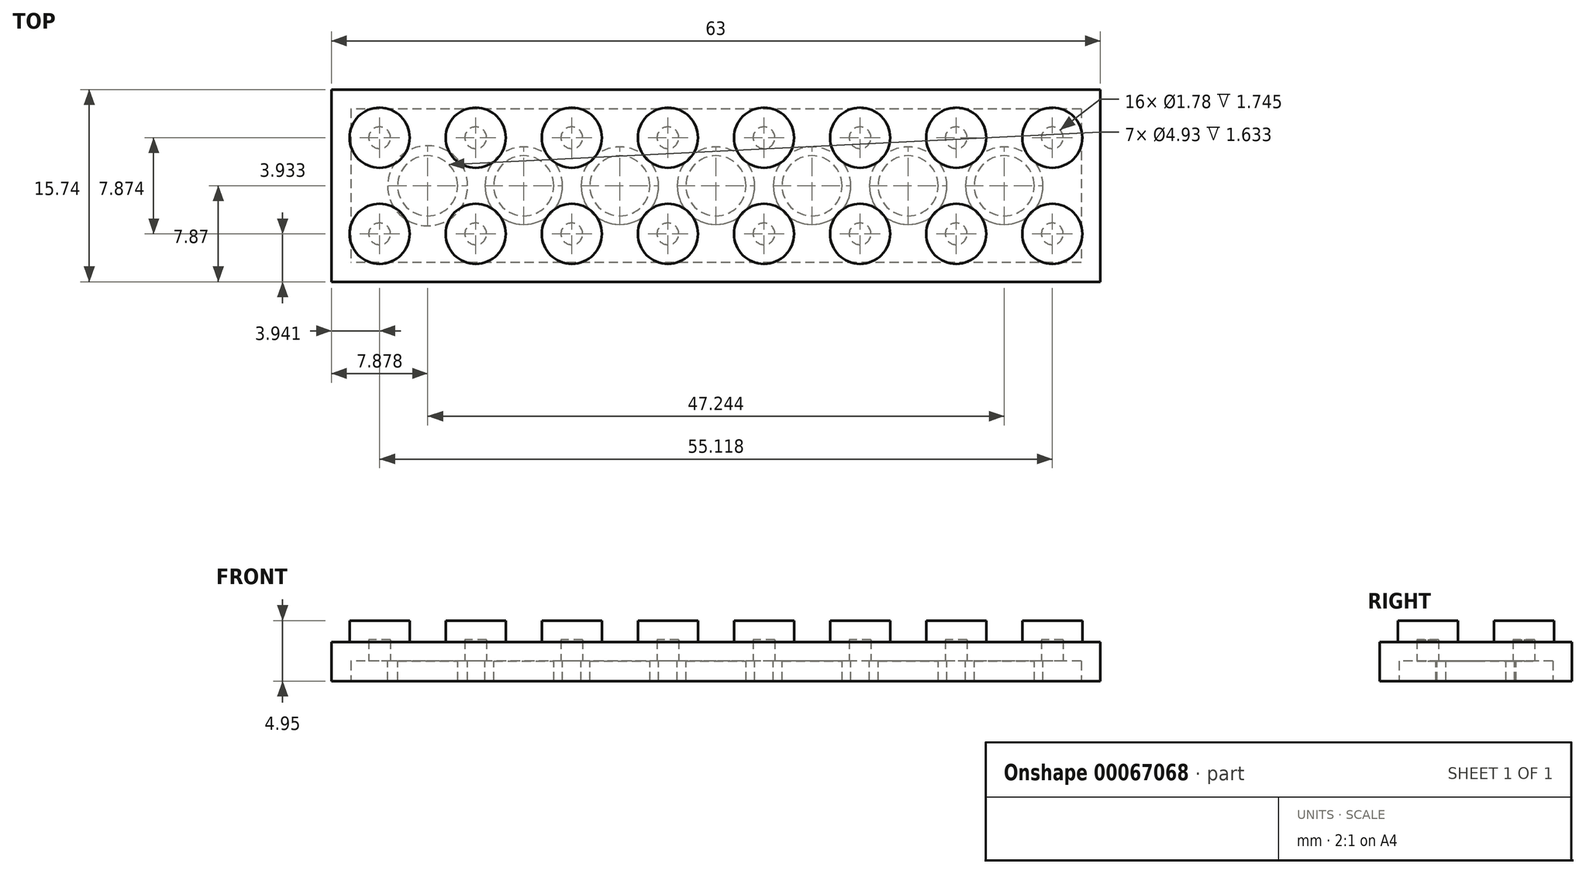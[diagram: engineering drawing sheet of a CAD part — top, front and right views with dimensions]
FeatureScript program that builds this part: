
annotation { "Feature Type Name" : "Feature", "Feature Type Description" : "" }
export const myFeature = defineFeature(function(context is Context, id is Id, definition is map)
    precondition{}
    {
        {
            var Q0;
            Q0=qCreatedBy(makeId("Top.planeOp"),FACE);
            var sketch = newSketch(context, id + "F0", { "sketchPlane" : qUnion([Q0])});
            skLineSegment(sketch, "E0.rect.bottom", {"start": v(31.5, 7.87) * mm, "end": v(-31.5, 7.87) * mm});
            skLineSegment(sketch, "E0.rect.top", {"start": v(31.5, -7.87) * mm, "end": v(-31.5, -7.87) * mm});
            skLineSegment(sketch, "E0.rect.left", {"start": v(31.5, 7.87) * mm, "end": v(31.5, -7.87) * mm});
            skLineSegment(sketch, "E0.rect.right", {"start": v(-31.5, 7.87) * mm, "end": v(-31.5, -7.87) * mm});
            skPoint(sketch, "E0.rect.middle", {"position": v(0, 0) * mm});
            skSolve(sketch);
        }
        {
            var Q0;
            Q0=makeQuery(id+"F0.imprint","IMPRINT",FACE,{"disambiguationData":[TD([[makeQuery(id+"F0.imprint","IMPRINT",EDGE,{"derivedFrom":sQuery(id+"F0.wireOp",EDGE,"E0.rect.bottom")}),1.0]])]});
            extrude(context, id + "F1", {"entities" : qUnion([Q0]), "depth" : 3.2 * mm});
        }
        {
            var Q0;
            Q0=qCreatedBy(makeId("Top.planeOp"),FACE);
            var sketch = newSketch(context, id + "F2", { "sketchPlane" : qUnion([Q0])});
            skCircle(sketch, "E1", {"center": v(-27.56, 3.94) * mm, "radius": 2.46 * mm});
            skCircle(sketch, "E2", {"center": v(-19.69, 3.94) * mm, "radius": 2.46 * mm});
            skCircle(sketch, "E3", {"center": v(-11.81, 3.94) * mm, "radius": 2.46 * mm});
            skCircle(sketch, "E4", {"center": v(-3.94, 3.94) * mm, "radius": 2.46 * mm});
            skCircle(sketch, "E5", {"center": v(-3.94, -3.94) * mm, "radius": 2.46 * mm});
            skCircle(sketch, "E6", {"center": v(-11.81, -3.94) * mm, "radius": 2.46 * mm});
            skCircle(sketch, "E7", {"center": v(-19.69, -3.94) * mm, "radius": 2.46 * mm});
            skCircle(sketch, "E8", {"center": v(-27.56, -3.94) * mm, "radius": 2.46 * mm});
            skCircle(sketch, "E9", {"center": v(3.94, 3.94) * mm, "radius": 2.46 * mm});
            skCircle(sketch, "E10", {"center": v(11.81, 3.94) * mm, "radius": 2.46 * mm});
            skCircle(sketch, "E11", {"center": v(11.81, -3.94) * mm, "radius": 2.46 * mm});
            skCircle(sketch, "E12", {"center": v(3.94, -3.94) * mm, "radius": 2.46 * mm});
            skCircle(sketch, "E13", {"center": v(19.69, 3.94) * mm, "radius": 2.46 * mm});
            skCircle(sketch, "E14", {"center": v(27.56, 3.94) * mm, "radius": 2.46 * mm});
            skCircle(sketch, "E15", {"center": v(19.69, -3.94) * mm, "radius": 2.46 * mm});
            skCircle(sketch, "E16", {"center": v(27.56, -3.94) * mm, "radius": 2.46 * mm});
            skSolve(sketch);
        }
        {
            var Q0;
            Q0=makeQuery(id+"F2.imprint","IMPRINT",FACE,{"disambiguationData":[TD([[makeQuery(id+"F2.imprint","IMPRINT",EDGE,{"derivedFrom":sQuery(id+"F2.wireOp",EDGE,"E14")}),1.0]])]});
            var Q1;
            Q1=makeQuery(id+"F2.imprint","IMPRINT",FACE,{"disambiguationData":[TD([[makeQuery(id+"F2.imprint","IMPRINT",EDGE,{"derivedFrom":sQuery(id+"F2.wireOp",EDGE,"E10")}),1.0]])]});
            var Q2;
            Q2=makeQuery(id+"F2.imprint","IMPRINT",FACE,{"disambiguationData":[TD([[makeQuery(id+"F2.imprint","IMPRINT",EDGE,{"derivedFrom":sQuery(id+"F2.wireOp",EDGE,"E13")}),1.0]])]});
            var Q3;
            Q3=makeQuery(id+"F2.imprint","IMPRINT",FACE,{"disambiguationData":[TD([[makeQuery(id+"F2.imprint","IMPRINT",EDGE,{"derivedFrom":sQuery(id+"F2.wireOp",EDGE,"E9")}),1.0]])]});
            var Q4;
            Q4=makeQuery(id+"F2.imprint","IMPRINT",FACE,{"disambiguationData":[TD([[makeQuery(id+"F2.imprint","IMPRINT",EDGE,{"derivedFrom":sQuery(id+"F2.wireOp",EDGE,"E4")}),1.0]])]});
            var Q5;
            Q5=makeQuery(id+"F2.imprint","IMPRINT",FACE,{"disambiguationData":[TD([[makeQuery(id+"F2.imprint","IMPRINT",EDGE,{"derivedFrom":sQuery(id+"F2.wireOp",EDGE,"E3")}),1.0]])]});
            var Q6;
            Q6=makeQuery(id+"F2.imprint","IMPRINT",FACE,{"disambiguationData":[TD([[makeQuery(id+"F2.imprint","IMPRINT",EDGE,{"derivedFrom":sQuery(id+"F2.wireOp",EDGE,"E2")}),1.0]])]});
            var Q7;
            Q7=makeQuery(id+"F2.imprint","IMPRINT",FACE,{"disambiguationData":[TD([[makeQuery(id+"F2.imprint","IMPRINT",EDGE,{"derivedFrom":sQuery(id+"F2.wireOp",EDGE,"E1")}),1.0]])]});
            var Q8;
            Q8=makeQuery(id+"F2.imprint","IMPRINT",FACE,{"disambiguationData":[TD([[makeQuery(id+"F2.imprint","IMPRINT",EDGE,{"derivedFrom":sQuery(id+"F2.wireOp",EDGE,"E8")}),1.0]])]});
            var Q9;
            Q9=makeQuery(id+"F2.imprint","IMPRINT",FACE,{"disambiguationData":[TD([[makeQuery(id+"F2.imprint","IMPRINT",EDGE,{"derivedFrom":sQuery(id+"F2.wireOp",EDGE,"E7")}),1.0]])]});
            var Q10;
            Q10=makeQuery(id+"F2.imprint","IMPRINT",FACE,{"disambiguationData":[TD([[makeQuery(id+"F2.imprint","IMPRINT",EDGE,{"derivedFrom":sQuery(id+"F2.wireOp",EDGE,"E6")}),1.0]])]});
            var Q11;
            Q11=makeQuery(id+"F2.imprint","IMPRINT",FACE,{"disambiguationData":[TD([[makeQuery(id+"F2.imprint","IMPRINT",EDGE,{"derivedFrom":sQuery(id+"F2.wireOp",EDGE,"E5")}),1.0]])]});
            var Q12;
            Q12=makeQuery(id+"F2.imprint","IMPRINT",FACE,{"disambiguationData":[TD([[makeQuery(id+"F2.imprint","IMPRINT",EDGE,{"derivedFrom":sQuery(id+"F2.wireOp",EDGE,"E12")}),1.0]])]});
            var Q13;
            Q13=makeQuery(id+"F2.imprint","IMPRINT",FACE,{"disambiguationData":[TD([[makeQuery(id+"F2.imprint","IMPRINT",EDGE,{"derivedFrom":sQuery(id+"F2.wireOp",EDGE,"E11")}),1.0]])]});
            var Q14;
            Q14=makeQuery(id+"F2.imprint","IMPRINT",FACE,{"disambiguationData":[TD([[makeQuery(id+"F2.imprint","IMPRINT",EDGE,{"derivedFrom":sQuery(id+"F2.wireOp",EDGE,"E15")}),1.0]])]});
            var Q15;
            Q15=makeQuery(id+"F2.imprint","IMPRINT",FACE,{"disambiguationData":[TD([[makeQuery(id+"F2.imprint","IMPRINT",EDGE,{"derivedFrom":sQuery(id+"F2.wireOp",EDGE,"E16")}),1.0]])]});
            extrude(context, id + "F3", {"entities" : qUnion([Q0, Q1, Q2, Q3, Q4, Q5, Q6, Q7, Q8, Q9, Q10, Q11, Q12, Q13, Q14, Q15]), "operationType" : NewBodyOperationType.ADD, "depth" : 4.95 * mm});
        }
        {
            var Q0;
            Q0=makeQuery(id+"F1.opExtrude","CAP_FACE",FACE,{"disambiguationData":[OSD([sQuery(id+"F0.wireOp",EDGE,"E0.rect.bottom"),sQuery(id+"F0.wireOp",EDGE,"E0.rect.top"),sQuery(id+"F0.wireOp",EDGE,"E0.rect.left"),sQuery(id+"F0.wireOp",EDGE,"E0.rect.right")])],"isStart":true});
            shell(context, id + "F4", {"entities" : qUnion([Q0]), "thickness" : 1.57 * mm});
        }
        {
            var Q0;
            Q0=makeQuery(id+"F4.opShell","OFFSET_FACE",FACE,{"disambiguationData":[OSD([sQuery(id+"F0.wireOp",EDGE,"E0.rect.bottom"),sQuery(id+"F0.wireOp",EDGE,"E0.rect.top"),sQuery(id+"F0.wireOp",EDGE,"E0.rect.left"),sQuery(id+"F0.wireOp",EDGE,"E0.rect.right")])]});
            var sketch = newSketch(context, id + "F5", { "sketchPlane" : qUnion([Q0])});
            skCircle(sketch, "E17", {"center": v(0, 0) * mm, "radius": 2.46 * mm});
            skLineSegment(sketch, "E18", {"start": v(0, 0) * mm, "end": v(7.87, 0) * mm});
            skLineSegment(sketch, "E19", {"start": v(7.87, 0) * mm, "end": v(15.75, 0) * mm});
            skLineSegment(sketch, "E20", {"start": v(15.75, 0) * mm, "end": v(23.62, 0) * mm});
            skLineSegment(sketch, "E21", {"start": v(0, 0) * mm, "end": v(-7.87, 0) * mm});
            skLineSegment(sketch, "E22", {"start": v(-7.87, 0) * mm, "end": v(-15.75, 0) * mm});
            skLineSegment(sketch, "E23", {"start": v(-15.75, 0) * mm, "end": v(-23.62, 0) * mm});
            skCircle(sketch, "E24", {"center": v(-7.87, 0) * mm, "radius": 2.46 * mm});
            skCircle(sketch, "E25", {"center": v(-15.75, 0) * mm, "radius": 2.46 * mm});
            skCircle(sketch, "E26", {"center": v(-23.62, 0) * mm, "radius": 2.46 * mm});
            skCircle(sketch, "E27", {"center": v(7.87, 0) * mm, "radius": 2.46 * mm});
            skCircle(sketch, "E28", {"center": v(15.75, 0) * mm, "radius": 2.46 * mm});
            skCircle(sketch, "E29", {"center": v(23.62, 0) * mm, "radius": 2.46 * mm});
            skCircle(sketch, "E30", {"center": v(-23.62, 0) * mm, "radius": 3.28 * mm});
            skCircle(sketch, "E31", {"center": v(-15.75, 0) * mm, "radius": 3.18 * mm});
            skCircle(sketch, "E32", {"center": v(-7.87, 0) * mm, "radius": 3.18 * mm});
            skCircle(sketch, "E33", {"center": v(0, 0) * mm, "radius": 3.18 * mm});
            skCircle(sketch, "E34", {"center": v(7.87, 0) * mm, "radius": 3.18 * mm});
            skCircle(sketch, "E35", {"center": v(15.75, 0) * mm, "radius": 3.18 * mm});
            skCircle(sketch, "E36", {"center": v(23.62, 0) * mm, "radius": 3.18 * mm});
            skSolve(sketch);
        }
        {
            var Q0;
            Q0=makeQuery(id+"F5.imprint","IMPRINT",FACE,{"disambiguationData":[TD([[makeQuery(id+"F5.imprint","IMPRINT",EDGE,{"derivedFrom":sQuery(id+"F5.wireOp",EDGE,"E26")}),-1.0]])]});
            var Q1;
            {var subQ0=sQuery(id+"F5.wireOp",EDGE,"E31");var subQ1=sQuery(id+"F5.wireOp",EDGE,"E22");var subQ2=makeQuery(id+"F5.imprint","INTERSECT",VERTEX,{"derivedFrom":[subQ1,subQ0]});Q1=makeQuery(id+"F5.imprint","IMPRINT",FACE,{"disambiguationData":[TD([[makeQuery(id+"F5.imprint","IMPRINT",EDGE,{"disambiguationData":[TD([[subQ2,-1.0]])],"derivedFrom":subQ1}),-1.0]])]});}
            var Q2;
            {var subQ0=sQuery(id+"F5.wireOp",EDGE,"E31");var subQ1=sQuery(id+"F5.wireOp",EDGE,"E22");var subQ2=makeQuery(id+"F5.imprint","INTERSECT",VERTEX,{"derivedFrom":[subQ1,subQ0]});Q2=makeQuery(id+"F5.imprint","IMPRINT",FACE,{"disambiguationData":[TD([[makeQuery(id+"F5.imprint","IMPRINT",EDGE,{"disambiguationData":[TD([[subQ2,-1.0]])],"derivedFrom":subQ1}),1.0]])]});}
            var Q3;
            {var subQ0=sQuery(id+"F5.wireOp",EDGE,"E32");var subQ1=sQuery(id+"F5.wireOp",EDGE,"E21");var subQ2=makeQuery(id+"F5.imprint","INTERSECT",VERTEX,{"derivedFrom":[subQ1,subQ0]});Q3=makeQuery(id+"F5.imprint","IMPRINT",FACE,{"disambiguationData":[TD([[makeQuery(id+"F5.imprint","IMPRINT",EDGE,{"disambiguationData":[TD([[subQ2,-1.0]])],"derivedFrom":subQ1}),1.0]])]});}
            var Q4;
            {var subQ0=sQuery(id+"F5.wireOp",EDGE,"E32");var subQ1=sQuery(id+"F5.wireOp",EDGE,"E21");var subQ2=makeQuery(id+"F5.imprint","INTERSECT",VERTEX,{"derivedFrom":[subQ1,subQ0]});Q4=makeQuery(id+"F5.imprint","IMPRINT",FACE,{"disambiguationData":[TD([[makeQuery(id+"F5.imprint","IMPRINT",EDGE,{"disambiguationData":[TD([[subQ2,-1.0]])],"derivedFrom":subQ1}),-1.0]])]});}
            var Q5;
            {var subQ0=sQuery(id+"F5.wireOp",EDGE,"E18");var subQ1=sQuery(id+"F5.wireOp",EDGE,"E17");var subQ2=makeQuery(id+"F5.imprint","INTERSECT",VERTEX,{"derivedFrom":[subQ1,subQ0]});Q5=makeQuery(id+"F5.imprint","IMPRINT",FACE,{"disambiguationData":[TD([[makeQuery(id+"F5.imprint","IMPRINT",EDGE,{"disambiguationData":[TD([[subQ2,-1.0]])],"derivedFrom":subQ1}),-1.0]])]});}
            var Q6;
            {var subQ0=sQuery(id+"F5.wireOp",EDGE,"E18");var subQ1=sQuery(id+"F5.wireOp",EDGE,"E17");var subQ2=makeQuery(id+"F5.imprint","INTERSECT",VERTEX,{"derivedFrom":[subQ1,subQ0]});Q6=makeQuery(id+"F5.imprint","IMPRINT",FACE,{"disambiguationData":[TD([[makeQuery(id+"F5.imprint","IMPRINT",EDGE,{"disambiguationData":[TD([[subQ2,1.0]])],"derivedFrom":subQ1}),-1.0]])]});}
            var Q7;
            {var subQ0=sQuery(id+"F5.wireOp",EDGE,"E34");var subQ1=sQuery(id+"F5.wireOp",EDGE,"E18");var subQ2=makeQuery(id+"F5.imprint","INTERSECT",VERTEX,{"derivedFrom":[subQ1,subQ0]});Q7=makeQuery(id+"F5.imprint","IMPRINT",FACE,{"disambiguationData":[TD([[makeQuery(id+"F5.imprint","IMPRINT",EDGE,{"disambiguationData":[TD([[subQ2,-1.0]])],"derivedFrom":subQ1}),-1.0]])]});}
            var Q8;
            {var subQ0=sQuery(id+"F5.wireOp",EDGE,"E34");var subQ1=sQuery(id+"F5.wireOp",EDGE,"E18");var subQ2=makeQuery(id+"F5.imprint","INTERSECT",VERTEX,{"derivedFrom":[subQ1,subQ0]});Q8=makeQuery(id+"F5.imprint","IMPRINT",FACE,{"disambiguationData":[TD([[makeQuery(id+"F5.imprint","IMPRINT",EDGE,{"disambiguationData":[TD([[subQ2,-1.0]])],"derivedFrom":subQ1}),1.0]])]});}
            var Q9;
            {var subQ0=sQuery(id+"F5.wireOp",EDGE,"E35");var subQ1=sQuery(id+"F5.wireOp",EDGE,"E19");var subQ2=makeQuery(id+"F5.imprint","INTERSECT",VERTEX,{"derivedFrom":[subQ1,subQ0]});Q9=makeQuery(id+"F5.imprint","IMPRINT",FACE,{"disambiguationData":[TD([[makeQuery(id+"F5.imprint","IMPRINT",EDGE,{"disambiguationData":[TD([[subQ2,-1.0]])],"derivedFrom":subQ1}),1.0]])]});}
            var Q10;
            {var subQ0=sQuery(id+"F5.wireOp",EDGE,"E35");var subQ1=sQuery(id+"F5.wireOp",EDGE,"E19");var subQ2=makeQuery(id+"F5.imprint","INTERSECT",VERTEX,{"derivedFrom":[subQ1,subQ0]});Q10=makeQuery(id+"F5.imprint","IMPRINT",FACE,{"disambiguationData":[TD([[makeQuery(id+"F5.imprint","IMPRINT",EDGE,{"disambiguationData":[TD([[subQ2,-1.0]])],"derivedFrom":subQ1}),-1.0]])]});}
            var Q11;
            Q11=makeQuery(id+"F5.imprint","IMPRINT",FACE,{"disambiguationData":[TD([[makeQuery(id+"F5.imprint","IMPRINT",EDGE,{"derivedFrom":sQuery(id+"F5.wireOp",EDGE,"E29")}),-1.0]])]});
            extrude(context, id + "F6", {"entities" : qUnion([Q0, Q1, Q2, Q3, Q4, Q5, Q6, Q7, Q8, Q9, Q10, Q11]), "operationType" : NewBodyOperationType.ADD, "depth" : 1.63 * mm});
        }
    });
